AUTODESK INVENTOR PART (.ipt)
format: ipt  version: 2023 (Build 270158000, 158)  size: 284,672 bytes
history: native  units: mm
features: reference x6, other x6, extrude x2, sketch x2, plane x1
ambient origin geometry x8: Origin, YZ Plane, XZ Plane, XY Plane, X Axis, Y Axis, Z Axis, Center Point
bodies: Solid1 (feature_tree)
feature tree (17):
  plane  "Work Plane1"
  extrude  "Extrusion1"  Depth=0.15mm
  extrude  "Extrusion2"  Depth=10.0mm
  sketch  "Sketch1"  dims[d0=10.15mm d1=0.15mm]
  reference  "Reference1"
  reference  "Reference2"
  reference  "Reference3"
  reference  "Reference4"
  reference  "Reference5"
  sketch  "Sketch2"  dims[d2=12.0mm d3=10.0mm d4=10.0mm d5=20.0mm d7=48.171mm d8=20.0mm d10=42.149mm d13=2.5mm d14=20.0mm d16=42.149mm d17=20.0mm d19=48.171mm d22=5.0mm d23=5.0mm d24=0.0mm d25=0.0mm d26=0.0mm d27=0.0mm]
  reference  "Reference6"
  parser-record x1  (decoder bookkeeping rows leaked as tree rows — omitted from the tree; the rows remain in map.json)
  other  "doorLockAssembly_V5.iam"
  other  "moulding:1"
  other  "pinion_V4:2"
  other  "pinion_V4:1"
  other  "rack_V3:1"
note: 1 file-system path scrubbed to <path> (originals preserved in map.json)
